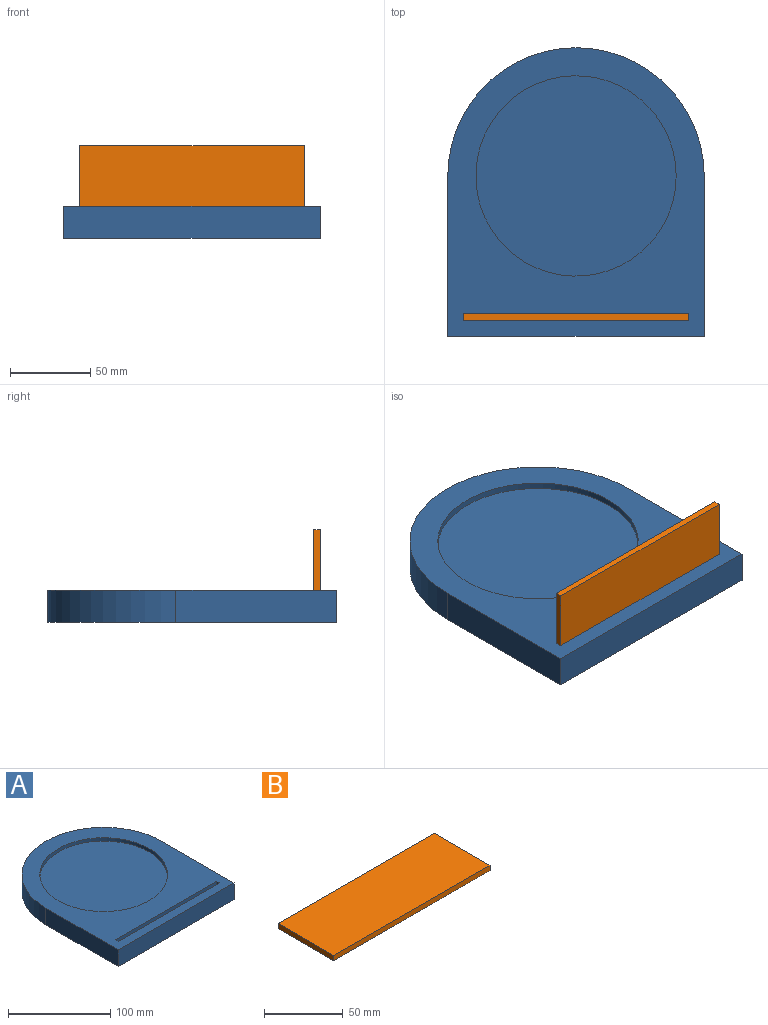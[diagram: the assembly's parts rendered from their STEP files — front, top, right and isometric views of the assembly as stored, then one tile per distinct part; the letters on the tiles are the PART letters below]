
ASSEMBLY  parts=2 mates=1
PART A: 13 faces, bbox 160x180x20 mm
  f0: plane 180x160mm, normal (0,0,1), area 13221.3mm2, adj f1,f2,f3,f4,f6,f8,f9,f10
  f1: plane 100x20mm, normal (-1,0,0), area 2000mm2, adj f0,f2,f4,f5
  f2: plane 160x20mm, normal (0,-1,0), area 3200mm2, adj f0,f1,f3,f5
  f3: plane 100x20mm, normal (1,0,0), area 2000mm2, adj f0,f2,f4,f5
  f4: cylinder r=80mm len=160mm, axis (0,0,-1), area 5026.5mm2, adj f0,f1,f3,f5
  f5: plane 180x160mm, normal (0,0,-1), area 26053.1mm2, adj f1,f2,f3,f4
  f6: cylinder r=62.5mm len=125mm, axis (0,0,1), area 1570.8mm2, adj f0,f7
  f7: plane 125x125mm, normal (0,0,1), area 12271.8mm2, adj f6
  f8: plane 140x12mm, normal (0,-1,0), area 1680mm2, adj f0,f9,f11,f12
  f9: plane 12x4mm, normal (1,0,0), area 48mm2, adj f0,f8,f10,f12
  f10: plane 140x12mm, normal (0,1,0), area 1680mm2, adj f0,f9,f11,f12
  f11: plane 12x4mm, normal (-1,0,0), area 48mm2, adj f0,f8,f10,f12
  f12: plane 140x4mm, normal (0,0,1), area 560mm2, adj f8,f9,f10,f11
PART B: 6 faces, bbox 140x50x4 mm
  f0: plane 140x4mm, normal (0,1,0), area 560mm2, adj f1,f3,f4,f5
  f1: plane 50x4mm, normal (-1,0,0), area 200mm2, adj f0,f2,f4,f5
  f2: plane 140x4mm, normal (0,-1,0), area 560mm2, adj f1,f3,f4,f5
  f3: plane 50x4mm, normal (1,0,0), area 200mm2, adj f0,f2,f4,f5
  f4: plane 140x50mm, normal (0,0,1), area 7000mm2, adj f0,f1,f2,f3
  f5: plane 140x50mm, normal (0,0,-1), area 7000mm2, adj f0,f1,f2,f3
PLACE A t=(-10.49,4.9,-14.45)mm
PLACE B rot(axis=(-1,0,0),90deg) t=(-80.49,-85.1,43.55)mm
MATE slider B.f0 <-> A.f12  axis (0,0,-1) through (-10.49,-83.1,-6.45)mm
